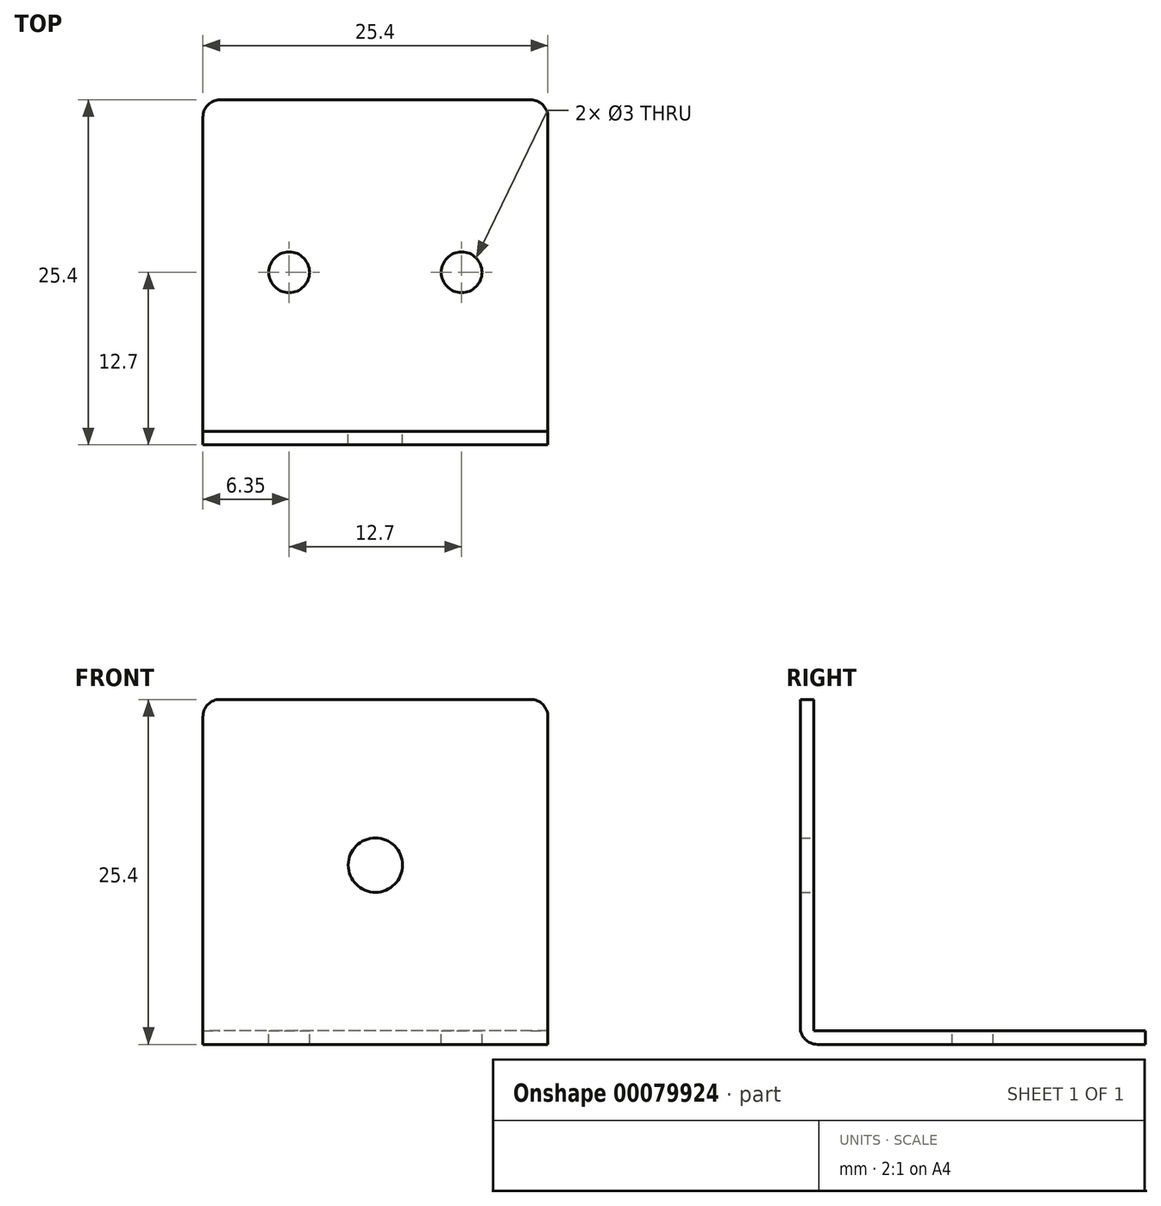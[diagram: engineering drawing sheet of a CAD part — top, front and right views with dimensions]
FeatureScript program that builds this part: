
annotation { "Feature Type Name" : "Feature", "Feature Type Description" : "" }
export const myFeature = defineFeature(function(context is Context, id is Id, definition is map)
    precondition{}
    {
        {
            var Q0;
            Q0=qCreatedBy(makeId("Front.planeOp"),FACE);
            var sketch = newSketch(context, id + "F0", { "sketchPlane" : qUnion([Q0])});
            skLineSegment(sketch, "E0.bottom", {"start": v(12.7, -12.2) * mm, "end": v(-12.7, -12.2) * mm});
            skLineSegment(sketch, "E0.top", {"start": v(12.7, 12.2) * mm, "end": v(-12.7, 12.2) * mm});
            skLineSegment(sketch, "E0.left", {"start": v(12.7, -12.2) * mm, "end": v(12.7, 12.2) * mm});
            skLineSegment(sketch, "E0.right", {"start": v(-12.7, -12.2) * mm, "end": v(-12.7, 12.2) * mm});
            skPoint(sketch, "E0.middle", {"position": v(0, 0) * mm});
            skCircle(sketch, "E1", {"center": v(0, 0) * mm, "radius": 2 * mm});
            skSolve(sketch);
        }
        {
            var Q0;
            Q0=makeQuery(id+"F0.imprint","IMPRINT",FACE,{"disambiguationData":[TD([[makeQuery(id+"F0.imprint","IMPRINT",EDGE,{"derivedFrom":sQuery(id+"F0.wireOp",EDGE,"E0.bottom")}),-1.0]])]});
            extrude(context, id + "F1", {"entities" : qUnion([Q0]), "depth" : 1 * mm});
        }
        {
            var Q0;
            Q0=makeQuery(id+"F1.opExtrude","SWEPT_EDGE",EDGE,{"disambiguationData":[OSD([sQuery(id+"F0.wireOp",EDGE,"E0.top"),sQuery(id+"F0.wireOp",EDGE,"E0.left")])]});
            var Q1;
            Q1=makeQuery(id+"F1.opExtrude","SWEPT_EDGE",EDGE,{"disambiguationData":[OSD([sQuery(id+"F0.wireOp",EDGE,"E0.top"),sQuery(id+"F0.wireOp",EDGE,"E0.right")])]});
            fillet(context, id + "F2", {"entities" : qUnion([Q0, Q1]), "radius" : 1.27 * mm, "tangentPropagation" : true, "allowEdgeOverflow" : false});
        }
        {
            var Q0;
            Q0=makeQuery(id+"F1.opExtrude","SWEPT_FACE",FACE,{"disambiguationData":[OSD([sQuery(id+"F0.wireOp",EDGE,"E0.bottom")])]});
            var sketch = newSketch(context, id + "F3", { "sketchPlane" : qUnion([Q0])});
            skLineSegment(sketch, "E2.bottom", {"start": v(12.7, 1) * mm, "end": v(-12.7, 1) * mm});
            skLineSegment(sketch, "E2.top", {"start": v(12.7, -24.4) * mm, "end": v(-12.7, -24.4) * mm});
            skLineSegment(sketch, "E2.left", {"start": v(12.7, 1) * mm, "end": v(12.7, -24.4) * mm});
            skLineSegment(sketch, "E2.right", {"start": v(-12.7, 1) * mm, "end": v(-12.7, -24.4) * mm});
            skLineSegment(sketch, "E3", {"start": v(0, 1) * mm, "end": v(0, -11.7) * mm, "construction": true});
            skPoint(sketch, "E3.endSnap0", {"position": v(0, 1) * mm});
            skCircle(sketch, "E4", {"center": v(-6.35, -11.7) * mm, "radius": 1.5 * mm});
            skCircle(sketch, "E5.MirrorC", {"center": v(6.35, -11.7) * mm, "radius": 1.5 * mm});
            skSolve(sketch);
        }
        {
            var Q0;
            {var subQ2=sQuery(id+"F3.wireOp",EDGE,"E2.top");Q0=makeQuery(id+"F3.imprint","IMPRINT",FACE,{"disambiguationData":[TD([[makeQuery(id+"F3.imprint","IMPRINT",EDGE,{"derivedFrom":subQ2}),-1.0]])]});}
            var Q1;
            {var subQ0=sQuery(id+"F3.wireOp",EDGE,"E2.bottom");Q1=makeQuery(id+"F3.imprint","IMPRINT",FACE,{"disambiguationData":[TD([[makeQuery(id+"F3.imprint","IMPRINT",EDGE,{"derivedFrom":subQ0}),1.0]])]});}
            extrude(context, id + "F4", {"entities" : qUnion([Q0, Q1]), "operationType" : NewBodyOperationType.ADD, "depth" : 1 * mm});
        }
        {
            var Q0;
            Q0=makeQuery(id+"F4.opExtrude","CAP_EDGE",EDGE,{"disambiguationData":[OSD([sQuery(id+"F3.wireOp",EDGE,"E2.bottom")])],"isStart":false});
            var Q1;
            Q1=makeQuery(id+"F4.opExtrude","SWEPT_EDGE",EDGE,{"disambiguationData":[OSD([sQuery(id+"F3.wireOp",EDGE,"E2.top"),sQuery(id+"F3.wireOp",EDGE,"E2.right")])]});
            var Q2;
            Q2=makeQuery(id+"F4.opExtrude","SWEPT_EDGE",EDGE,{"disambiguationData":[OSD([sQuery(id+"F3.wireOp",EDGE,"E2.top"),sQuery(id+"F3.wireOp",EDGE,"E2.left")])]});
            fillet(context, id + "F5", {"entities" : qUnion([Q0, Q1, Q2]), "radius" : 1.27 * mm, "tangentPropagation" : true, "allowEdgeOverflow" : false});
        }
    });
